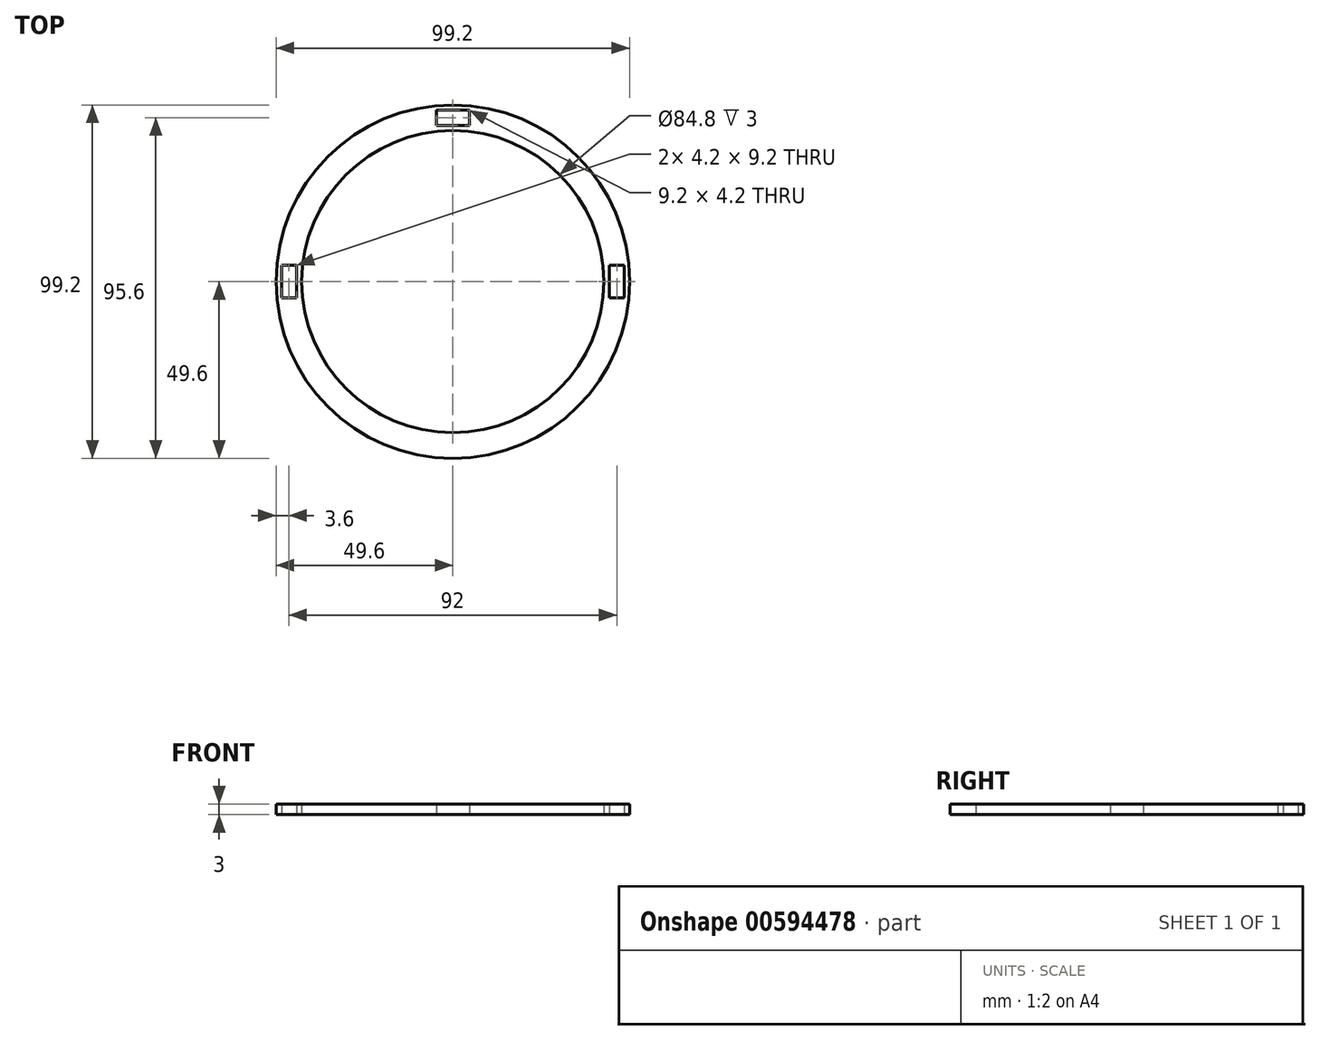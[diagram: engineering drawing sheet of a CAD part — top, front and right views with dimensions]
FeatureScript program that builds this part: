
annotation { "Feature Type Name" : "Feature", "Feature Type Description" : "" }
export const myFeature = defineFeature(function(context is Context, id is Id, definition is map)
    precondition{}
    {
        {
            var Q0;
            Q0=qCreatedBy(makeId("Top.planeOp"),FACE);
            var sketch = newSketch(context, id + "F0", { "sketchPlane" : qUnion([Q0])});
            skCircle(sketch, "E0", {"center": v(0, 0) * mm, "radius": 42.4 * mm});
            skCircle(sketch, "E1", {"center": v(0, 0) * mm, "radius": 49.6 * mm});
            skLineSegment(sketch, "E2", {"start": v(-49.6, 0) * mm, "end": v(-42.4, 0) * mm, "construction": true});
            skLineSegment(sketch, "E3", {"start": v(0, 49.6) * mm, "end": v(0, 42.4) * mm, "construction": true});
            skLineSegment(sketch, "E4", {"start": v(49.6, 0) * mm, "end": v(42.4, 0) * mm, "construction": true});
            skLineSegment(sketch, "E5.bottom", {"start": v(-43.9, -4.6) * mm, "end": v(-48.1, -4.6) * mm});
            skLineSegment(sketch, "E5.top", {"start": v(-43.9, 4.6) * mm, "end": v(-48.1, 4.6) * mm});
            skLineSegment(sketch, "E5.left", {"start": v(-43.9, -4.6) * mm, "end": v(-43.9, 4.6) * mm});
            skLineSegment(sketch, "E5.right", {"start": v(-48.1, -4.6) * mm, "end": v(-48.1, 4.6) * mm});
            skPoint(sketch, "E5.middle", {"position": v(-46, 0) * mm});
            skLineSegment(sketch, "E6.bottom", {"start": v(-4.6, 43.9) * mm, "end": v(4.6, 43.9) * mm});
            skLineSegment(sketch, "E6.top", {"start": v(-4.6, 48.1) * mm, "end": v(4.6, 48.1) * mm});
            skLineSegment(sketch, "E6.left", {"start": v(-4.6, 43.9) * mm, "end": v(-4.6, 48.1) * mm});
            skLineSegment(sketch, "E6.right", {"start": v(4.6, 43.9) * mm, "end": v(4.6, 48.1) * mm});
            skPoint(sketch, "E6.middle", {"position": v(0, 46) * mm});
            skLineSegment(sketch, "E7.bottom", {"start": v(48.1, -4.6) * mm, "end": v(43.9, -4.6) * mm});
            skLineSegment(sketch, "E7.top", {"start": v(48.1, 4.6) * mm, "end": v(43.9, 4.6) * mm});
            skLineSegment(sketch, "E7.left", {"start": v(48.1, -4.6) * mm, "end": v(48.1, 4.6) * mm});
            skLineSegment(sketch, "E7.right", {"start": v(43.9, -4.6) * mm, "end": v(43.9, 4.6) * mm});
            skPoint(sketch, "E7.middle", {"position": v(46, 0) * mm});
            skCircle(sketch, "E8", {"center": v(0, 0) * mm, "radius": 46 * mm, "construction": true});
            skSolve(sketch);
        }
        {
            var Q0;
            Q0=qSketchRegion(id+"F0",true);
            extrude(context, id + "F1", {"entities" : qUnion([Q0]), "depth" : 3 * mm});
        }
    });
